# Revit family: Storage-Teknion-LWBWS_Byward_Wall_Shelves-R2019
name_source: partatom
category: Furniture
units: mm (PartAtom-declared; Revit-internal decimal feet)

## family parameters
Always vertical = Yes
Cut with Voids When Loaded = No
OmniClass Number = 23.40.20.00
OmniClass Title = General Furniture and Specialties
Room Calculation Point = No
Shared = Yes
Work Plane-Based = No

## types (4) — shared parameters
Assembly Code = E2020200
Manufacturer = Teknion
Manufacturer Fax = 416.661.4586
Part Number = LWBWS
Product Documentation Link = https://assets.teknion.com
Product Line = Byward
Product Page URL = https://www.teknion.com
Series = Byward
Sustainability Data = https://www.teknion.com
URL = www.teknion.com
Unit Weight URL = http://www.teknion.com
Warranty = http://www.teknion.com

## per-type parameters (varying)
| type | Bottom Sliding Tray | Description | Model | Upper Shelf |
| Lower Shelf with Tray | Yes | Byward, Wall Shelves, Lower Shelf with Tray, 10" Height, 4" Depth | LWBWSB1004__ | No |
| Lower Shelf with Dividers | Yes | Byward, Wall Shelves, Lower Shelf with Dividers, 10" Height, 4" Depth | LWBWSC1004__ | No |
| Left Hooks, Upper Shelf | No | Byward, Wall Shelves, Left Hooks, Upper Shelf, 10" Height, 4" Depth | LWBWSL1004__ | Yes |
| Right Hooks, Upper Shelf | No | Byward, Wall Shelves, Right Hooks, Upper Shelf, 10" Height, 4" Depth | LWBWSR1004__ | Yes |

type visibility flags: 4 boolean params named "<type name>" — each type sets only its own to Yes (folded from table)

## geometry (parser evidence)
native form markers: Sweep x4
no freeform markers — native parametric forms only
